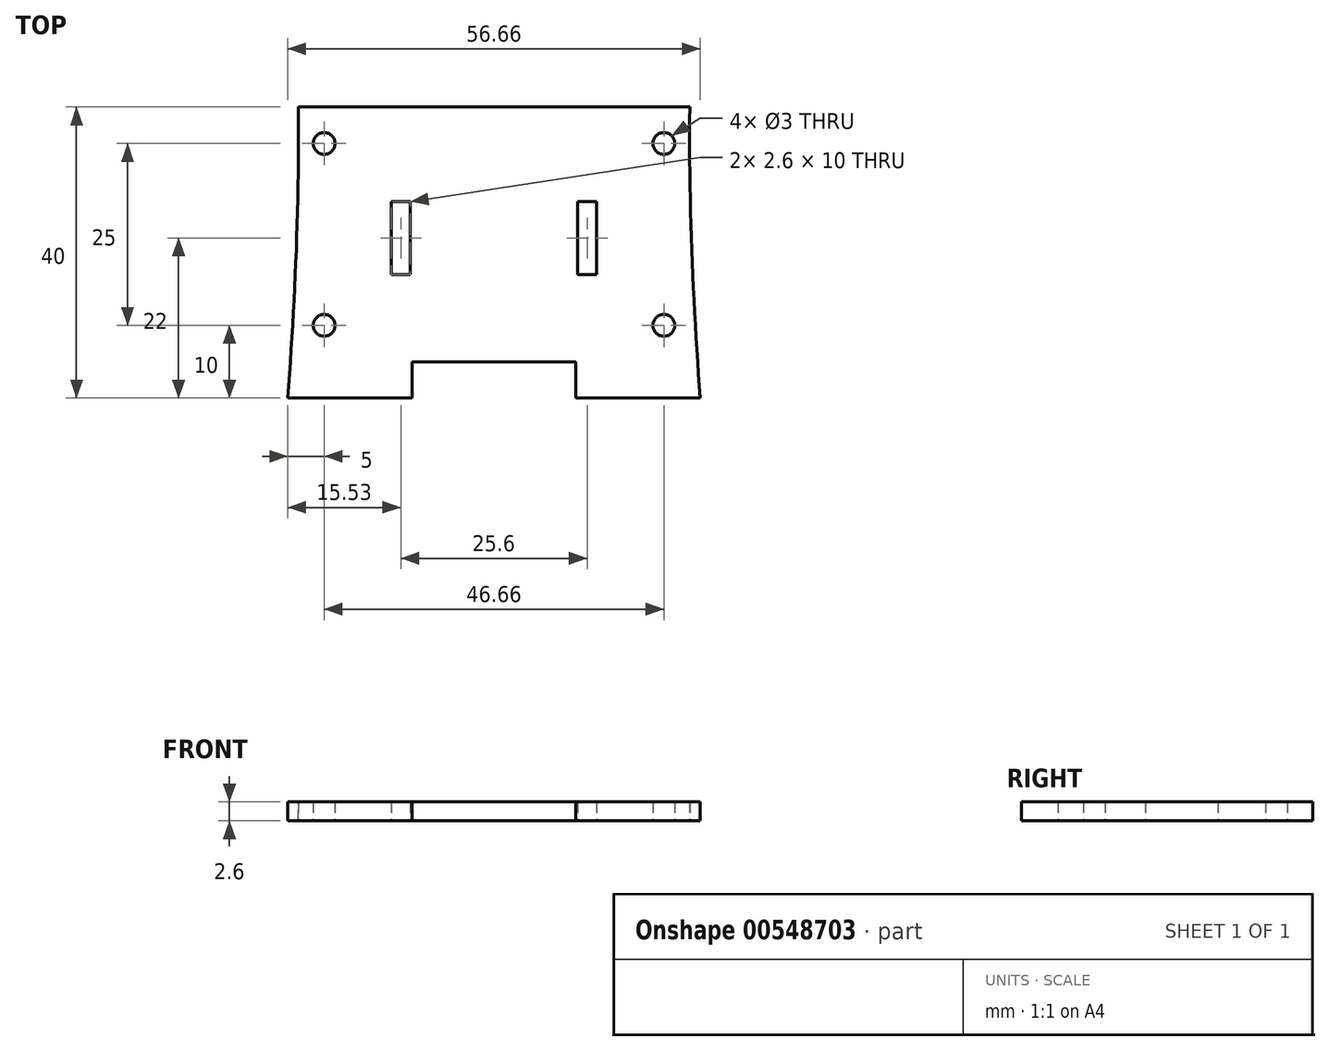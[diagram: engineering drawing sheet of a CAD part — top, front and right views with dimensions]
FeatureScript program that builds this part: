
annotation { "Feature Type Name" : "Feature", "Feature Type Description" : "" }
export const myFeature = defineFeature(function(context is Context, id is Id, definition is map)
    precondition{}
    {
        {
            assignVariable(context, id + "F0", {"variableType" : VariableType.LENGTH, "name" : "MaterialThickness", "lengthValue" : 2.6 * mm});
        }
        {
            var Q0;
            Q0=qCreatedBy(makeId("Top.planeOp"),FACE);
            var sketch = newSketch(context, id + "F1", { "sketchPlane" : qUnion([Q0])});
            skFitSpline(sketch, "E0", {"points": [v(-28.75, -160.5) * mm, v(-26.88, -117.5) * mm, v(-30.25, -64) * mm, v(-35.38, 0) * mm, v(-19.75, 76) * mm, v(0, 92) * mm], "startDerivative": vector(18.48, 223.68) * mm, "endDerivative": vector(112.8, 0.96) * mm});
            skLineSegment(sketch, "E1", {"start": v(0, 0) * mm, "end": v(0, 240.15) * mm, "construction": true});
            skFitSpline(sketch, "E2.MirrorCS", {"points": [v(28.75, -160.5) * mm, v(26.88, -117.5) * mm, v(30.25, -64) * mm, v(35.38, 0) * mm, v(19.75, 76) * mm, v(0, 92) * mm], "startDerivative": vector(-18.48, 223.68) * mm, "endDerivative": vector(-112.8, 0.96) * mm});
            skLineSegment(sketch, "E3", {"start": v(0, 0) * mm, "end": v(0, -344.13) * mm, "construction": true});
            skLineSegment(sketch, "E4", {"start": v(-28.75, -160.5) * mm, "end": v(28.75, -160.5) * mm});
            skLineSegment(sketch, "E5.bottom", {"start": v(14.1, -138.2) * mm, "end": v(11.5, -138.2) * mm});
            skLineSegment(sketch, "E5.top", {"start": v(14.1, -128.2) * mm, "end": v(11.5, -128.2) * mm});
            skLineSegment(sketch, "E5.left", {"start": v(14.1, -138.2) * mm, "end": v(14.1, -128.2) * mm});
            skLineSegment(sketch, "E5.right", {"start": v(11.5, -138.2) * mm, "end": v(11.5, -128.2) * mm});
            skPoint(sketch, "E5.middle", {"position": v(12.8, -133.2) * mm});
            skLineSegment(sketch, "E6.MirrorCS", {"start": v(-11.5, -138.2) * mm, "end": v(-11.5, -128.2) * mm});
            skLineSegment(sketch, "E7.MirrorCS", {"start": v(-14.1, -128.2) * mm, "end": v(-11.5, -128.2) * mm});
            skLineSegment(sketch, "E8.MirrorCS", {"start": v(-14.1, -138.2) * mm, "end": v(-14.1, -128.2) * mm});
            skLineSegment(sketch, "E9.MirrorCS", {"start": v(-14.1, -138.2) * mm, "end": v(-11.5, -138.2) * mm});
            skLineSegment(sketch, "E10", {"start": v(0, -160.5) * mm, "end": v(0, -155.2) * mm});
            skLineSegment(sketch, "E11", {"start": v(0, -155.2) * mm, "end": v(28.33, -155.2) * mm});
            skLineSegment(sketch, "E12", {"start": v(0, -155.2) * mm, "end": v(-28.33, -155.2) * mm});
            skLineSegment(sketch, "E13", {"start": v(0, -155.2) * mm, "end": v(0, -115.2) * mm});
            skLineSegment(sketch, "E14", {"start": v(0, -115.2) * mm, "end": v(26.9, -115.2) * mm});
            skLineSegment(sketch, "E15", {"start": v(0, -115.2) * mm, "end": v(-26.9, -115.2) * mm});
            skLineSegment(sketch, "E16.bottom", {"start": v(0, -155.2) * mm, "end": v(11.25, -155.2) * mm});
            skLineSegment(sketch, "E16.top", {"start": v(0, -150.2) * mm, "end": v(11.25, -150.2) * mm});
            skLineSegment(sketch, "E16.left", {"start": v(0, -155.2) * mm, "end": v(0, -150.2) * mm});
            skLineSegment(sketch, "E16.right", {"start": v(11.25, -155.2) * mm, "end": v(11.25, -150.2) * mm});
            skLineSegment(sketch, "E17.MirrorCS", {"start": v(0, -150.2) * mm, "end": v(-11.25, -150.2) * mm});
            skLineSegment(sketch, "E18.MirrorCS", {"start": v(-11.25, -155.2) * mm, "end": v(-11.25, -150.2) * mm});
            skLineSegment(sketch, "E19", {"start": v(23.33, -155.2) * mm, "end": v(23.33, -145.2) * mm});
            skLineSegment(sketch, "E20", {"start": v(23.33, -145.2) * mm, "end": v(23.33, -120.2) * mm});
            skCircle(sketch, "E21", {"center": v(23.33, -120.2) * mm, "radius": 1.5 * mm});
            skCircle(sketch, "E22", {"center": v(23.33, -145.2) * mm, "radius": 1.5 * mm});
            skLineSegment(sketch, "E23", {"start": v(28.33, -155.2) * mm, "end": v(23.33, -155.2) * mm});
            skCircle(sketch, "E24.MirrorC", {"center": v(-23.33, -120.2) * mm, "radius": 1.5 * mm});
            skCircle(sketch, "E25.MirrorC", {"center": v(-23.33, -145.2) * mm, "radius": 1.5 * mm});
            skSolve(sketch);
        }
        {
            var Q0;
            Q0=makeQuery(id+"F1.imprint","IMPRINT",FACE,{"disambiguationData":[TD([[makeQuery(id+"F1.imprint","IMPRINT",EDGE,{"derivedFrom":sQuery(id+"F1.wireOp",EDGE,"E5.bottom")}),1.0]])]});
            var Q1;
            Q1=makeQuery(id+"F1.imprint","IMPRINT",FACE,{"disambiguationData":[TD([[makeQuery(id+"F1.imprint","IMPRINT",EDGE,{"derivedFrom":sQuery(id+"F1.wireOp",EDGE,"E6.MirrorCS")}),-1.0]])]});
            extrude(context, id + "F2", {"entities" : qUnion([Q0, Q1]), "depth" : getVariable(context, 'MaterialThickness') / 2, "offsetDistance" : 25 * mm, "hasSecondDirection" : true, "secondDirectionOppositeDirection" : true, "secondDirectionDepth" : getVariable(context, 'MaterialThickness') / 2});
        }
        {
            var Q0;
            Q0=makeQuery(id+"F2.opExtrude","CAP_FACE",FACE,{"disambiguationData":[OSD([sQuery(id+"F1.wireOp",EDGE,"E0"),sQuery(id+"F1.wireOp",EDGE,"E2.MirrorCS"),sQuery(id+"F1.wireOp",EDGE,"E4"),sQuery(id+"F1.wireOp",EDGE,"E5.bottom"),sQuery(id+"F1.wireOp",EDGE,"E5.top"),sQuery(id+"F1.wireOp",EDGE,"E5.left"),sQuery(id+"F1.wireOp",EDGE,"E5.right"),sQuery(id+"F1.wireOp",EDGE,"E6.MirrorCS"),sQuery(id+"F1.wireOp",EDGE,"E7.MirrorCS"),sQuery(id+"F1.wireOp",EDGE,"E8.MirrorCS"),sQuery(id+"F1.wireOp",EDGE,"E9.MirrorCS")])],"isStart":false});
            var sketch = newSketch(context, id + "F3", { "sketchPlane" : qUnion([Q0])});
            skLineSegment(sketch, "E26.bottom", {"start": v(27.69, 8.25) * mm, "end": v(35.38, 8.25) * mm});
            skLineSegment(sketch, "E26.top", {"start": v(27.69, -6.25) * mm, "end": v(35.38, -6.25) * mm});
            skLineSegment(sketch, "E26.left", {"start": v(27.69, 8.25) * mm, "end": v(27.69, -6.25) * mm});
            skLineSegment(sketch, "E27.bottom", {"start": v(35.38, 8.25) * mm, "end": v(39.69, 8.25) * mm});
            skLineSegment(sketch, "E27.top", {"start": v(35.38, -6.25) * mm, "end": v(39.69, -6.25) * mm});
            skLineSegment(sketch, "E27.right", {"start": v(39.69, 8.25) * mm, "end": v(39.69, -6.25) * mm});
            skLineSegment(sketch, "E28", {"start": v(0, 0) * mm, "end": v(0, 50) * mm, "construction": true});
            skLineSegment(sketch, "E29.MirrorCS", {"start": v(-27.69, 8.25) * mm, "end": v(-35.38, 8.25) * mm});
            skLineSegment(sketch, "E30.MirrorCS", {"start": v(-35.38, -6.25) * mm, "end": v(-39.69, -6.25) * mm});
            skLineSegment(sketch, "E31.MirrorCS", {"start": v(-27.69, -6.25) * mm, "end": v(-35.38, -6.25) * mm});
            skLineSegment(sketch, "E32.MirrorCS", {"start": v(-27.69, 8.25) * mm, "end": v(-27.69, -6.25) * mm});
            skLineSegment(sketch, "E33.MirrorCS", {"start": v(-35.38, 8.25) * mm, "end": v(-39.69, 8.25) * mm});
            skLineSegment(sketch, "E34.MirrorCS", {"start": v(-39.69, 8.25) * mm, "end": v(-39.69, -6.25) * mm});
            skSolve(sketch);
        }
        {
            var Q0;
            {var subQ3=sQuery(id+"F3.wireOp",EDGE,"E26.bottom");Q0=makeQuery(id+"F3.imprint","IMPRINT",FACE,{"disambiguationData":[TD([[makeQuery(id+"F3.imprint","IMPRINT",EDGE,{"derivedFrom":subQ3}),-1.0]])]});}
            var Q1;
            {var subQ1=sQuery(id+"F3.wireOp",EDGE,"E29.MirrorCS");Q1=makeQuery(id+"F3.imprint","IMPRINT",FACE,{"disambiguationData":[TD([[makeQuery(id+"F3.imprint","IMPRINT",EDGE,{"derivedFrom":subQ1}),1.0]])]});}
            extrude(context, id + "F4", {"entities" : qUnion([Q0, Q1]), "operationType" : NewBodyOperationType.REMOVE, "endBound" : BoundingType.THROUGH_ALL, "oppositeDirection" : true, "depth" : 25 * mm, "offsetDistance" : 25 * mm});
        }
    });
